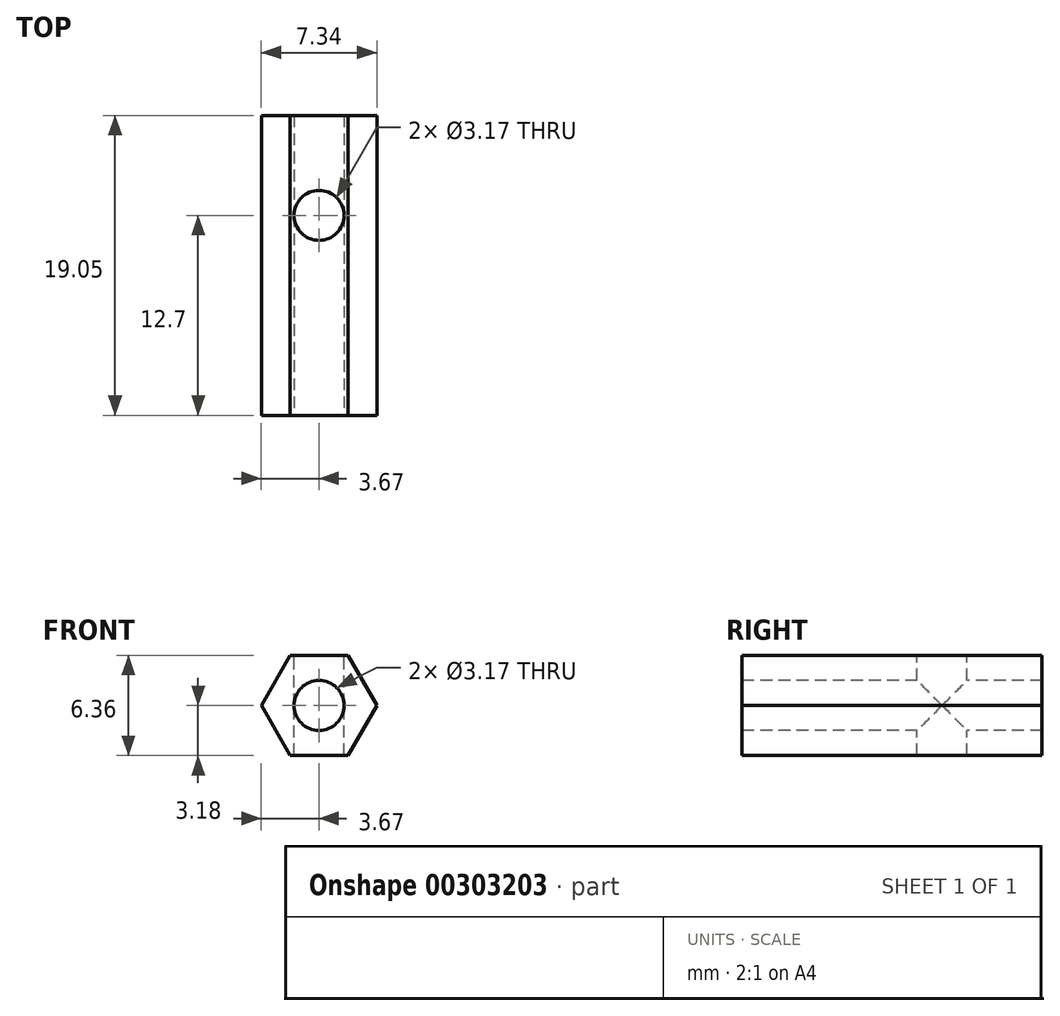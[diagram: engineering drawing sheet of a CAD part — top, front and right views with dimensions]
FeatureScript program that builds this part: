
annotation { "Feature Type Name" : "Feature", "Feature Type Description" : "" }
export const myFeature = defineFeature(function(context is Context, id is Id, definition is map)
    precondition{}
    {
        {
            var Q0;
            Q0=qCreatedBy(makeId("Front.planeOp"),FACE);
            var sketch = newSketch(context, id + "F0", { "sketchPlane" : qUnion([Q0])});
            skCircle(sketch, "E0.cCircle", {"center": v(0, 0) * mm, "radius": 3.18 * mm, "construction": true});
            skLineSegment(sketch, "E0.0", {"start": v(-1.83, 3.18) * mm, "end": v(1.83, 3.18) * mm});
            skLineSegment(sketch, "E0.1", {"start": v(1.83, 3.18) * mm, "end": v(3.67, 0) * mm});
            skLineSegment(sketch, "E0.2", {"start": v(3.67, 0) * mm, "end": v(1.83, -3.17) * mm});
            skLineSegment(sketch, "E0.3", {"start": v(1.83, -3.17) * mm, "end": v(-1.83, -3.18) * mm});
            skLineSegment(sketch, "E0.4", {"start": v(-1.83, -3.18) * mm, "end": v(-3.67, 0) * mm});
            skLineSegment(sketch, "E0.5", {"start": v(-3.67, 0) * mm, "end": v(-1.83, 3.18) * mm});
            skPoint(sketch, "E0.0.midPoint", {"position": v(0, 3.18) * mm});
            skSolve(sketch);
        }
        {
            var Q0;
            Q0 = qSketchRegion(id + "F0", true);
            extrude(context, id + "F1", {"entities" : qUnion([Q0]), "depth" : 19.05 * mm});
        }
        {
            var Q0;
            Q0=makeQuery(id+"F1.opExtrude","SWEPT_FACE",FACE,{"disambiguationData":[OSD([sQuery(id+"F0.wireOp",EDGE,"E0.0")])]});
            var sketch = newSketch(context, id + "F2", { "sketchPlane" : qUnion([Q0])});
            skCircle(sketch, "E1", {"center": v(0, -6.35) * mm, "radius": 1.59 * mm});
            skSolve(sketch);
        }
        {
            var Q0;
            Q0 = qSketchRegion(id + "F2", true);
            extrude(context, id + "F3", {"entities" : qUnion([Q0]), "operationType" : NewBodyOperationType.REMOVE, "endBound" : BoundingType.THROUGH_ALL, "oppositeDirection" : true, "depth" : 25.4 * mm});
        }
        {
            var Q0;
            Q0=makeQuery(id+"F1.opExtrude","CAP_FACE",FACE,{"disambiguationData":[OSD([sQuery(id+"F0.wireOp",EDGE,"E0.0"),sQuery(id+"F0.wireOp",EDGE,"E0.1"),sQuery(id+"F0.wireOp",EDGE,"E0.2"),sQuery(id+"F0.wireOp",EDGE,"E0.3"),sQuery(id+"F0.wireOp",EDGE,"E0.4"),sQuery(id+"F0.wireOp",EDGE,"E0.5")])],"isStart":false});
            var sketch = newSketch(context, id + "F4", { "sketchPlane" : qUnion([Q0])});
            skCircle(sketch, "E2", {"center": v(0, 0) * mm, "radius": 1.59 * mm});
            skSolve(sketch);
        }
        {
            var Q0;
            Q0 = qSketchRegion(id + "F4", true);
            extrude(context, id + "F5", {"entities" : qUnion([Q0]), "operationType" : NewBodyOperationType.REMOVE, "endBound" : BoundingType.THROUGH_ALL, "oppositeDirection" : true, "depth" : 25.4 * mm});
        }
    });
